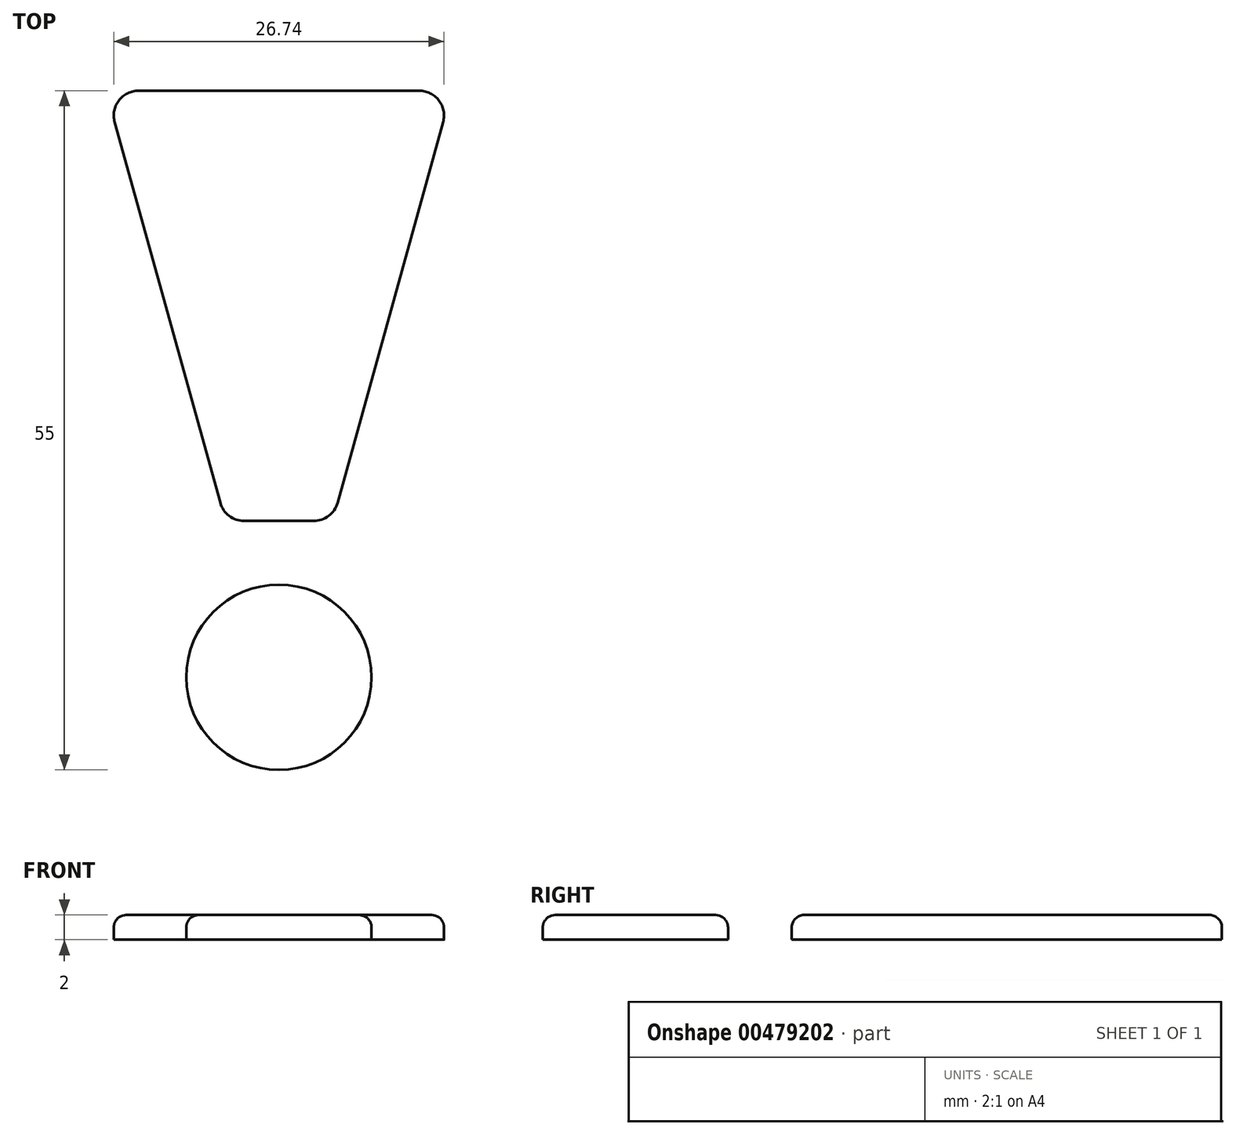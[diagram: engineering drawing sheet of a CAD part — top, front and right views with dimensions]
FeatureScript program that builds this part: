
annotation { "Feature Type Name" : "Feature", "Feature Type Description" : "" }
export const myFeature = defineFeature(function(context is Context, id is Id, definition is map)
    precondition{}
    {
        {
            var Q0;
            Q0=qCreatedBy(makeId("Top.planeOp"),FACE);
            var sketch = newSketch(context, id + "F0", { "sketchPlane" : qUnion([Q0])});
            skCircle(sketch, "E0", {"center": v(0, 0) * mm, "radius": 7.5 * mm});
            skLineSegment(sketch, "E1", {"start": v(0, 47.5) * mm, "end": v(-11.37, 47.5) * mm});
            skLineSegment(sketch, "E2", {"start": v(-13.3, 44.97) * mm, "end": v(-4.75, 14.13) * mm});
            skLineSegment(sketch, "E3", {"start": v(-2.82, 12.66) * mm, "end": v(0, 12.66) * mm});
            skLineSegment(sketch, "E4.MirrorCS", {"start": v(2.82, 12.66) * mm, "end": v(0, 12.66) * mm});
            skLineSegment(sketch, "E5.MirrorCS", {"start": v(13.3, 44.97) * mm, "end": v(4.75, 14.13) * mm});
            skLineSegment(sketch, "E6.MirrorCS", {"start": v(0, 47.5) * mm, "end": v(11.37, 47.5) * mm});
            skPoint(sketch, "E7.visualSharp", {"position": v(-14, 47.5) * mm});
            skArc(sketch, "E7.filletArc", {"start": v(-11.37, 47.5) * mm, "mid": v(-12.96, 46.71) * mm, "end": v(-13.3, 44.97) * mm});
            skPoint(sketch, "E8.visualSharp", {"position": v(14, 47.5) * mm});
            skArc(sketch, "E8.filletArc", {"start": v(13.3, 44.97) * mm, "mid": v(12.96, 46.71) * mm, "end": v(11.37, 47.5) * mm});
            skPoint(sketch, "E9.visualSharp", {"position": v(-4.34, 12.66) * mm});
            skArc(sketch, "E9.filletArc", {"start": v(-4.75, 14.13) * mm, "mid": v(-4.03, 13.07) * mm, "end": v(-2.82, 12.66) * mm});
            skPoint(sketch, "E10.visualSharp", {"position": v(4.34, 12.66) * mm});
            skArc(sketch, "E10.filletArc", {"start": v(2.82, 12.66) * mm, "mid": v(4.03, 13.07) * mm, "end": v(4.75, 14.13) * mm});
            skSolve(sketch);
        }
        {
            var Q0;
            Q0=makeQuery(id+"F0.imprint","IMPRINT",FACE,{"disambiguationData":[TD([[makeQuery(id+"F0.imprint","IMPRINT",EDGE,{"derivedFrom":sQuery(id+"F0.wireOp",EDGE,"E0")}),1.0]])]});
            var Q1;
            Q1=makeQuery(id+"F0.imprint","IMPRINT",FACE,{"disambiguationData":[TD([[makeQuery(id+"F0.imprint","IMPRINT",EDGE,{"derivedFrom":sQuery(id+"F0.wireOp",EDGE,"E1")}),1.0]])]});
            extrude(context, id + "F1", {"entities" : qUnion([Q0, Q1]), "depth" : 2 * mm});
        }
        {
            var Q0;
            Q0=makeQuery(id+"F1.opExtrude","CAP_EDGE",EDGE,{"disambiguationData":[OSD([sQuery(id+"F0.wireOp",EDGE,"E2")])],"isStart":false});
            var Q1;
            Q1=makeQuery(id+"F1.opExtrude","CAP_EDGE",EDGE,{"disambiguationData":[OSD([sQuery(id+"F0.wireOp",EDGE,"E0")])],"isStart":false});
            fillet(context, id + "F2", {"entities" : qUnion([Q0, Q1]), "radius" : 1 * mm, "tangentPropagation" : true, "allowEdgeOverflow" : false});
        }
    });
